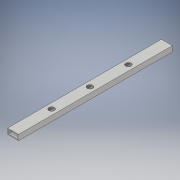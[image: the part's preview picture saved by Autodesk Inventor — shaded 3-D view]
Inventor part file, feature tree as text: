
AUTODESK INVENTOR PART (.ipt)
format: ipt  version: 2019 (Build 230136000, 136)  size: 115,712 bytes
history: native  units: in
note: dims shown in document units (in); Inventor stores cm internally (conversion verified against a paired STEP export)
features: extrude x2, sketch x2
ambient origin geometry x8: Origin, YZ Plane, XZ Plane, XY Plane, X Axis, Y Axis, Z Axis, Center Point
bodies: Solid1 (feature_tree)
feature tree (4):
  extrude  "Extrusion1"  Depth=1.0in
  extrude  "Extrusion2"  Depth=28.0in TaperAngle=0.0deg
  sketch  "Sketch1"  dims[d0=2.0in d1=1.0in]
  sketch  "Sketch2"  dims[d2=0.125in d3=28.0in d4=0.0in d5=1.0in d6=1.0in d7=0.0in]
